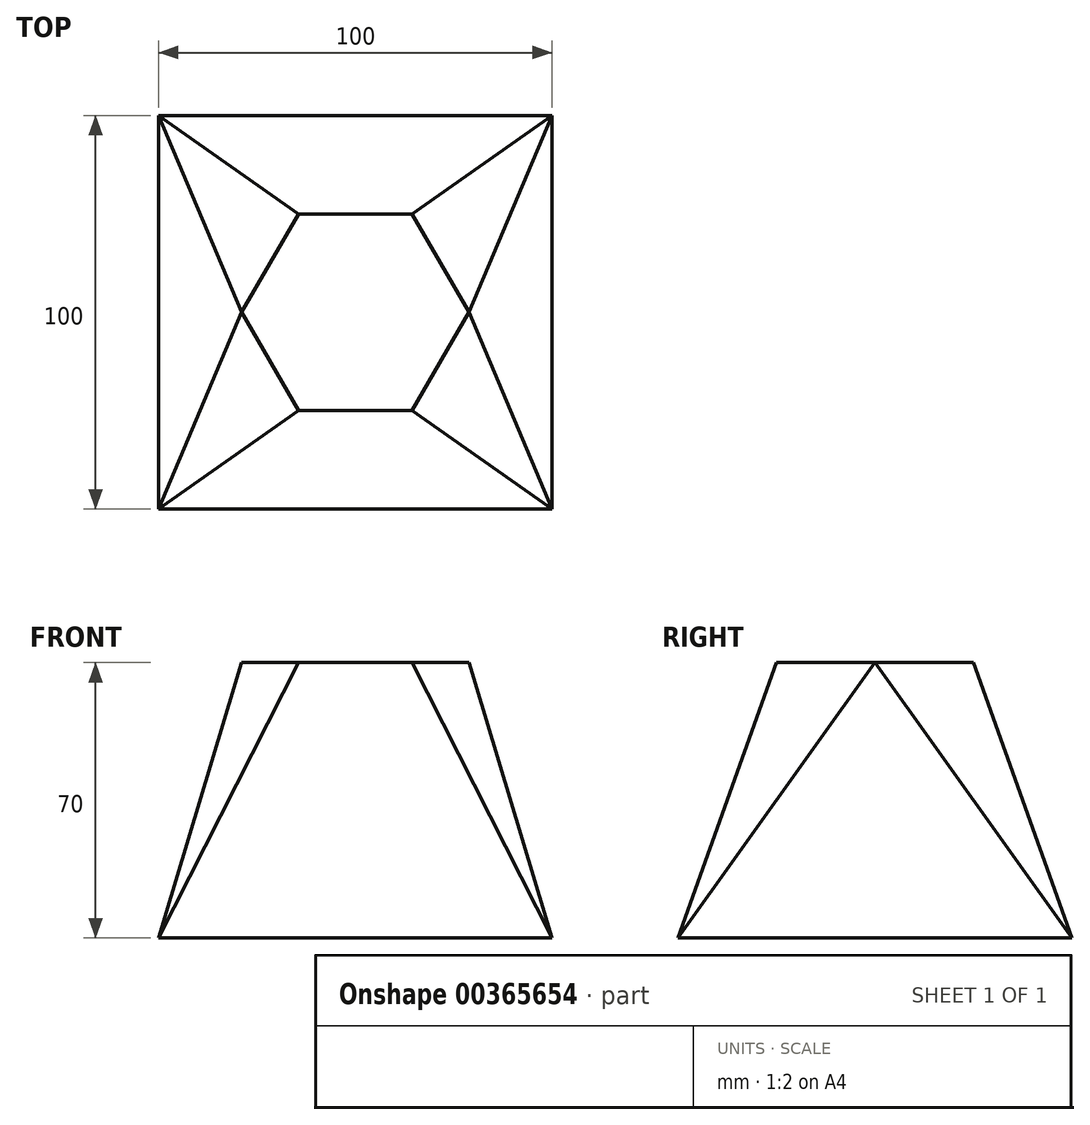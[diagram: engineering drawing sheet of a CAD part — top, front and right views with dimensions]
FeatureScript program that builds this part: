
annotation { "Feature Type Name" : "Feature", "Feature Type Description" : "" }
export const myFeature = defineFeature(function(context is Context, id is Id, definition is map)
    precondition{}
    {
        {
            var Q0;
            Q0=qCreatedBy(makeId("Top.planeOp"),FACE);
            var sketch = newSketch(context, id + "F0", { "sketchPlane" : qUnion([Q0])});
            skLineSegment(sketch, "E0.bottom", {"start": v(50, 50) * mm, "end": v(-50, 50) * mm});
            skLineSegment(sketch, "E0.top", {"start": v(50, -50) * mm, "end": v(-50, -50) * mm});
            skLineSegment(sketch, "E0.left", {"start": v(50, 50) * mm, "end": v(50, -50) * mm});
            skLineSegment(sketch, "E0.right", {"start": v(-50, 50) * mm, "end": v(-50, -50) * mm});
            skPoint(sketch, "E0.middle", {"position": v(0, 0) * mm});
            skSolve(sketch);
        }
        {
            var Q0;
            Q0=qCreatedBy(makeId("Top.planeOp"),FACE);
            cPlane(context, id + "F1", {"entities" : qUnion([Q0]), "cplaneType" : CPlaneType.OFFSET, "offset" : 70 * mm, "width" : 150 * mm, "height" : 150 * mm});
        }
        {
            var Q0;
            Q0=qCreatedBy(id+"F1.planeOp",FACE);
            var sketch = newSketch(context, id + "F2", { "sketchPlane" : qUnion([Q0])});
            skCircle(sketch, "E1.cCircle", {"center": v(0, 0) * mm, "radius": 25 * mm, "construction": true});
            skLineSegment(sketch, "E1.0", {"start": v(-14.43, 25) * mm, "end": v(14.43, 25) * mm});
            skLineSegment(sketch, "E1.1", {"start": v(14.43, 25) * mm, "end": v(28.87, 0) * mm});
            skLineSegment(sketch, "E1.2", {"start": v(28.87, 0) * mm, "end": v(14.43, -25) * mm});
            skLineSegment(sketch, "E1.3", {"start": v(14.43, -25) * mm, "end": v(-14.43, -25) * mm});
            skLineSegment(sketch, "E1.4", {"start": v(-14.43, -25) * mm, "end": v(-28.87, 0) * mm});
            skLineSegment(sketch, "E1.5", {"start": v(-28.87, 0) * mm, "end": v(-14.43, 25) * mm});
            skPoint(sketch, "E1.0.midPoint", {"position": v(0, 25) * mm});
            skLineSegment(sketch, "E2", {"start": v(-14.43, 25) * mm, "end": v(-14.43, -25) * mm});
            skLineSegment(sketch, "E3", {"start": v(14.43, 25) * mm, "end": v(14.43, -25) * mm});
            skSolve(sketch);
        }
        {
            var Q0;
            Q0=makeQuery(id+"F0.imprint","IMPRINT",FACE,{"disambiguationData":[TD([[makeQuery(id+"F0.imprint","IMPRINT",EDGE,{"derivedFrom":sQuery(id+"F0.wireOp",EDGE,"E0.bottom")}),1.0]])]});
            var Q1;
            Q1=makeQuery(id+"F2.imprint","IMPRINT",FACE,{"disambiguationData":[TD([[makeQuery(id+"F2.imprint","IMPRINT",EDGE,{"derivedFrom":sQuery(id+"F2.wireOp",EDGE,"E1.0")}),-1.0]])]});
            loft(context, id + "F3", {"sheetProfilesArray" : [{ "sheetProfileEntities" : qUnion([Q0]) }, { "sheetProfileEntities" : qUnion([Q1]) }]});
        }
        {
            var Q1;
            Q1=makeQuery(id+"F2.imprint","IMPRINT",FACE,{"disambiguationData":[TD([[makeQuery(id+"F2.imprint","IMPRINT",EDGE,{"derivedFrom":sQuery(id+"F2.wireOp",EDGE,"E1.1")}),-1.0]])]});
            var Q2;
            Q2=makeQuery(id+"F3.opLoft","MID_CAP_VERTEX",VERTEX,{"disambiguationData":[OSD([sQuery(id+"F0.wireOp",EDGE,"E0.top"),sQuery(id+"F0.wireOp",EDGE,"E0.left")])],"capPos":0.0});
            loft(context, id + "F4", {"operationType" : NewBodyOperationType.ADD, "sheetProfilesArray" : [{ "sheetProfileEntities" : qUnion([Q1]) }, { "sheetProfileEntities" : qUnion([Q2]) }]});
        }
        {
            var Q1;
            Q1=makeQuery(id+"F2.imprint","IMPRINT",FACE,{"disambiguationData":[TD([[makeQuery(id+"F2.imprint","IMPRINT",EDGE,{"derivedFrom":sQuery(id+"F2.wireOp",EDGE,"E1.1")}),-1.0]])]});
            var Q2;
            Q2=makeQuery(id+"F3.opLoft","MID_CAP_VERTEX",VERTEX,{"disambiguationData":[OSD([sQuery(id+"F0.wireOp",EDGE,"E0.bottom"),sQuery(id+"F0.wireOp",EDGE,"E0.left")])],"capPos":0.0});
            loft(context, id + "F5", {"operationType" : NewBodyOperationType.ADD, "sheetProfilesArray" : [{ "sheetProfileEntities" : qUnion([Q1]) }, { "sheetProfileEntities" : qUnion([Q2]) }]});
        }
        {
            var Q1;
            Q1=makeQuery(id+"F5.opLoft","SWEPT_FACE",FACE,{"disambiguationData":[OSD([sQuery(id+"F2.wireOp",EDGE,"E1.1"),sQuery(id+"F2.wireOp",EDGE,"E1.2"),sQuery(id+"F2.wireOp",EDGE,"E1.3"),sQuery(id+"F2.wireOp",EDGE,"E3")])]});
            var Q2;
            Q2=makeQuery(id+"F4.opLoft","SWEPT_FACE",FACE,{"disambiguationData":[OSD([sQuery(id+"F2.wireOp",EDGE,"E1.0"),sQuery(id+"F2.wireOp",EDGE,"E1.1"),sQuery(id+"F2.wireOp",EDGE,"E1.2"),sQuery(id+"F2.wireOp",EDGE,"E3")])]});
            var Q3;
            Q3=makeQuery(id+"F3.opLoft","MID_CAP_EDGE",EDGE,{"disambiguationData":[OSD([sQuery(id+"F0.wireOp",EDGE,"E0.bottom"),sQuery(id+"F0.wireOp",EDGE,"E0.top"),sQuery(id+"F0.wireOp",EDGE,"E0.left")])],"capPos":0.0});
            loft(context, id + "F6", {"operationType" : NewBodyOperationType.ADD, "addGuides" : true, "sheetProfilesArray" : [{ "sheetProfileEntities" : qUnion([Q1]) }, { "sheetProfileEntities" : qUnion([Q2]) }], "guidesArray" : [{ "guideEntities" : qUnion([Q3]), "guideDerivativeType" : LoftGuideDerivativeType.DEFAULT, "guideDerivativeMagnitude" : 1 }]});
        }
        {
            var Q1;
            Q1=makeQuery(id+"F2.imprint","IMPRINT",FACE,{"disambiguationData":[TD([[makeQuery(id+"F2.imprint","IMPRINT",EDGE,{"derivedFrom":sQuery(id+"F2.wireOp",EDGE,"E1.4")}),-1.0]])]});
            var Q2;
            Q2=makeQuery(id+"F3.opLoft","MID_CAP_VERTEX",VERTEX,{"disambiguationData":[OSD([sQuery(id+"F0.wireOp",EDGE,"E0.bottom"),sQuery(id+"F0.wireOp",EDGE,"E0.right")])],"capPos":0.0});
            loft(context, id + "F7", {"operationType" : NewBodyOperationType.ADD, "sheetProfilesArray" : [{ "sheetProfileEntities" : qUnion([Q1]) }, { "sheetProfileEntities" : qUnion([Q2]) }]});
        }
        {
            var Q1;
            Q1=makeQuery(id+"F2.imprint","IMPRINT",FACE,{"disambiguationData":[TD([[makeQuery(id+"F2.imprint","IMPRINT",EDGE,{"derivedFrom":sQuery(id+"F2.wireOp",EDGE,"E1.4")}),-1.0]])]});
            var Q2;
            Q2=makeQuery(id+"F3.opLoft","MID_CAP_VERTEX",VERTEX,{"disambiguationData":[OSD([sQuery(id+"F0.wireOp",EDGE,"E0.top"),sQuery(id+"F0.wireOp",EDGE,"E0.right")])],"capPos":0.0});
            loft(context, id + "F8", {"operationType" : NewBodyOperationType.ADD, "sheetProfilesArray" : [{ "sheetProfileEntities" : qUnion([Q1]) }, { "sheetProfileEntities" : qUnion([Q2]) }]});
        }
        {
            var Q1;
            Q1=makeQuery(id+"F7.opLoft","SWEPT_FACE",FACE,{"disambiguationData":[OSD([sQuery(id+"F2.wireOp",EDGE,"E1.3"),sQuery(id+"F2.wireOp",EDGE,"E1.4"),sQuery(id+"F2.wireOp",EDGE,"E1.5"),sQuery(id+"F2.wireOp",EDGE,"E2")])]});
            var Q2;
            Q2=makeQuery(id+"F8.opLoft","SWEPT_FACE",FACE,{"disambiguationData":[OSD([sQuery(id+"F2.wireOp",EDGE,"E1.0"),sQuery(id+"F2.wireOp",EDGE,"E1.4"),sQuery(id+"F2.wireOp",EDGE,"E1.5"),sQuery(id+"F2.wireOp",EDGE,"E2")])]});
            var Q3;
            Q3=makeQuery(id+"F3.opLoft","MID_CAP_EDGE",EDGE,{"disambiguationData":[OSD([sQuery(id+"F0.wireOp",EDGE,"E0.bottom"),sQuery(id+"F0.wireOp",EDGE,"E0.top"),sQuery(id+"F0.wireOp",EDGE,"E0.right")])],"capPos":0.0});
            loft(context, id + "F9", {"operationType" : NewBodyOperationType.ADD, "addGuides" : true, "sheetProfilesArray" : [{ "sheetProfileEntities" : qUnion([Q1]) }, { "sheetProfileEntities" : qUnion([Q2]) }], "guidesArray" : [{ "guideEntities" : qUnion([Q3]), "guideDerivativeType" : LoftGuideDerivativeType.DEFAULT, "guideDerivativeMagnitude" : 1 }]});
        }
    });
